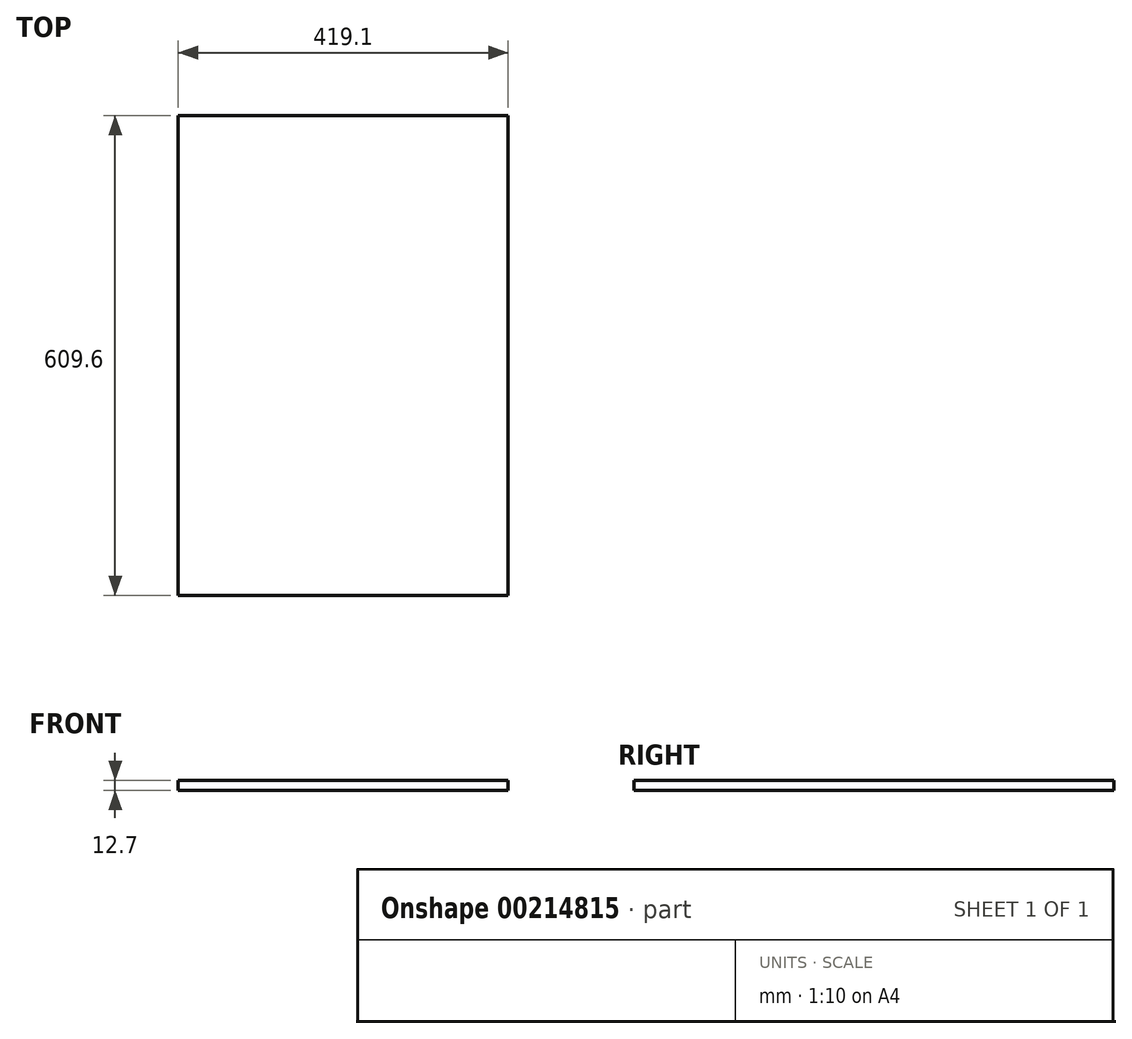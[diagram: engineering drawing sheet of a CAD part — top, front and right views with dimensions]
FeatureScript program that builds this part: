
annotation { "Feature Type Name" : "Feature", "Feature Type Description" : "" }
export const myFeature = defineFeature(function(context is Context, id is Id, definition is map)
    precondition{}
    {
        {
            var Q0;
            Q0=qCreatedBy(makeId("Top.planeOp"),FACE);
            var sketch = newSketch(context, id + "F0", { "sketchPlane" : qUnion([Q0])});
            skLineSegment(sketch, "E0.bottom", {"start": v(0, 0) * mm, "end": v(419.1, 0) * mm});
            skLineSegment(sketch, "E0.top", {"start": v(0, -609.6) * mm, "end": v(419.1, -609.6) * mm});
            skLineSegment(sketch, "E0.left", {"start": v(0, 0) * mm, "end": v(0, -609.6) * mm});
            skLineSegment(sketch, "E0.right", {"start": v(419.1, 0) * mm, "end": v(419.1, -609.6) * mm});
            skSolve(sketch);
        }
        {
            var Q0;
            Q0=makeQuery(id+"F0.imprint","IMPRINT",FACE,{"disambiguationData":[TD([[makeQuery(id+"F0.imprint","IMPRINT",EDGE,{"derivedFrom":sQuery(id+"F0.wireOp",EDGE,"E0.bottom")}),-1.0]])]});
            extrude(context, id + "F1", {"entities" : qUnion([Q0]), "depth" : 12.7 * mm});
        }
    });
